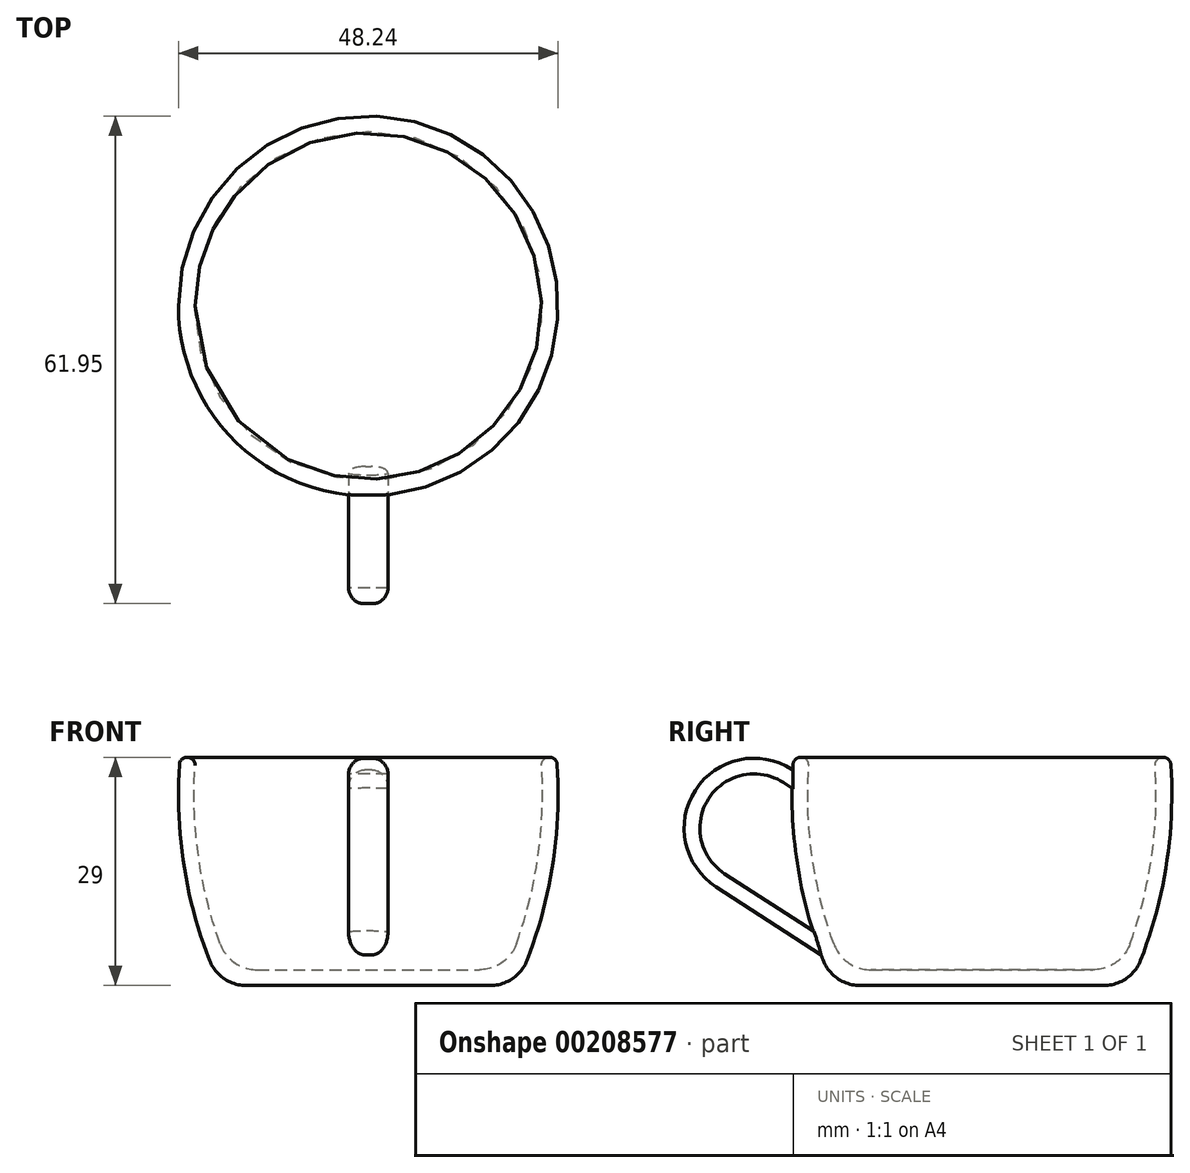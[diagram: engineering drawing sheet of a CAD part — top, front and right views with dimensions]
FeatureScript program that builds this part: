
annotation { "Feature Type Name" : "Feature", "Feature Type Description" : "" }
export const myFeature = defineFeature(function(context is Context, id is Id, definition is map)
    precondition{}
    {
        {
            var Q0;
            Q0=qCreatedBy(makeId("Right.planeOp"),FACE);
            var sketch = newSketch(context, id + "F0", { "sketchPlane" : qUnion([Q0])});
            skLineSegment(sketch, "E0", {"start": v(0, 0) * mm, "end": v(-15.5, 0) * mm});
            skArc(sketch, "E1", {"start": v(-24, 28.07) * mm, "mid": v(-23.45, 15.41) * mm, "end": v(-20.16, 3.18) * mm});
            skPoint(sketch, "E2.visualSharp", {"position": v(-18.8, 0) * mm});
            skArc(sketch, "E2.filletArc", {"start": v(-20.16, 3.18) * mm, "mid": v(-18.32, 0.87) * mm, "end": v(-15.5, 0) * mm});
            skLineSegment(sketch, "E3.0", {"start": v(0, 2) * mm, "end": v(-14.11, 2) * mm});
            skArc(sketch, "E4.0", {"start": v(-22, 27.93) * mm, "mid": v(-21.58, 16.46) * mm, "end": v(-18.82, 5.3) * mm});
            skArc(sketch, "E5.filletArc", {"start": v(-18.82, 5.3) * mm, "mid": v(-16.99, 2.9) * mm, "end": v(-14.11, 2) * mm});
            skArc(sketch, "E6", {"start": v(-24, 28.07) * mm, "mid": v(-22.94, 29) * mm, "end": v(-22, 27.93) * mm});
            skLineSegment(sketch, "E7", {"start": v(0, 2) * mm, "end": v(0, 0) * mm});
            skLineSegment(sketch, "E8", {"start": v(0, -19.62) * mm, "end": v(0, 44.5) * mm, "construction": true});
            skSolve(sketch);
        }
        {
            var Q0;
            Q0=makeQuery(id+"F0.imprint","IMPRINT",FACE,{"disambiguationData":[TD([[makeQuery(id+"F0.imprint","IMPRINT",EDGE,{"derivedFrom":sQuery(id+"F0.wireOp",EDGE,"E0")}),-1.0]])]});
            var Q1;
            Q1=sQuery(id+"F0.wireOp",EDGE,"E8");
            revolve(context, id + "F1", {"entities" : qUnion([Q0]), "axis" : qUnion([Q1]), "revolveType" : RevolveType.FULL});
        }
        {
            var Q0;
            Q0=qCreatedBy(makeId("Right.planeOp"),FACE);
            var sketch = newSketch(context, id + "F2", { "sketchPlane" : qUnion([Q0])});
            skLineSegment(sketch, "E9", {"start": v(-20.37, 3.74) * mm, "end": v(-33.82, 12.42) * mm});
            skArc(sketch, "E10", {"start": v(-33.82, 12.42) * mm, "mid": v(-36.5, 24.87) * mm, "end": v(-24.03, 27.53) * mm});
            skSolve(sketch);
        }
        {
            var Q0;
            Q0=sQuery(id+"F2.wireOp",EDGE,"E10");
            var Q1;
            Q1=sQuery(id+"F2.wireOp",VERTEX,"E10.end");
            cPlane(context, id + "F3", {"entities" : qUnion([Q0, Q1]), "cplaneType" : CPlaneType.CURVE_POINT, "offset" : 25 * mm, "width" : 150 * mm, "height" : 150 * mm});
        }
        {
            var Q0;
            Q0=qCreatedBy(id+"F3.planeOp",FACE);
            var sketch = newSketch(context, id + "F4", { "sketchPlane" : qUnion([Q0])});
            skPoint(sketch, "E11.0", {"position": v(0, 9.99) * mm});
            skLineSegment(sketch, "E12.bottom", {"start": v(-2.5, 9.99) * mm, "end": v(2.5, 9.99) * mm});
            skLineSegment(sketch, "E12.top", {"start": v(-2.5, 7.99) * mm, "end": v(2.5, 7.99) * mm});
            skLineSegment(sketch, "E12.left", {"start": v(-2.5, 9.99) * mm, "end": v(-2.5, 7.99) * mm});
            skLineSegment(sketch, "E12.right", {"start": v(2.5, 9.99) * mm, "end": v(2.5, 7.99) * mm});
            skSolve(sketch);
        }
        {
            var Q0;
            Q0=makeQuery(id+"F4.imprint","IMPRINT",FACE,{"disambiguationData":[TD([[makeQuery(id+"F4.imprint","IMPRINT",EDGE,{"derivedFrom":sQuery(id+"F4.wireOp",EDGE,"E12.bottom")}),-1.0]])]});
            var Q1;
            Q1=makeQuery(id+"F1.opRevolve","SWEPT_FACE",FACE,{"disambiguationData":[OSD([sQuery(id+"F0.wireOp",EDGE,"E1")])]});
            extrude(context, id + "F5", {"entities" : qUnion([Q0]), "operationType" : NewBodyOperationType.ADD, "endBound" : BoundingType.UP_TO_SURFACE, "endBoundEntityFace" : qUnion([Q1]), "depth" : 25 * mm});
        }
        {
            var Q0;
            Q0=makeQuery(id+"F4.imprint","IMPRINT",FACE,{"disambiguationData":[TD([[makeQuery(id+"F4.imprint","IMPRINT",EDGE,{"derivedFrom":sQuery(id+"F4.wireOp",EDGE,"E12.bottom")}),-1.0]])]});
            var Q1;
            Q1=sQuery(id+"F2.wireOp",EDGE,"E10");
            var Q2;
            Q2=sQuery(id+"F2.wireOp",EDGE,"E9");
            sweep(context, id + "F6", {"operationType" : NewBodyOperationType.ADD, "profiles" : qUnion([Q0]), "path" : qUnion([Q1, Q2])});
        }
        {
            var Q0;
            Q0=makeQuery(id+"F6.opSweep","SWEPT_EDGE",EDGE,{"disambiguationData":[OSD([sQuery(id+"F2.wireOp",EDGE,"E10"),sQuery(id+"F4.wireOp",EDGE,"E12.bottom"),sQuery(id+"F4.wireOp",EDGE,"E12.right")])]});
            var Q1;
            Q1=makeQuery(id+"F6.opSweep","SWEPT_EDGE",EDGE,{"disambiguationData":[OSD([sQuery(id+"F2.wireOp",EDGE,"E10"),sQuery(id+"F4.wireOp",EDGE,"E12.bottom"),sQuery(id+"F4.wireOp",EDGE,"E12.left")])]});
            fillet(context, id + "F7", {"entities" : qUnion([Q0, Q1]), "radius" : 2 * mm, "tangentPropagation" : true, "allowEdgeOverflow" : false});
        }
    });
